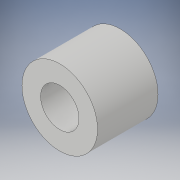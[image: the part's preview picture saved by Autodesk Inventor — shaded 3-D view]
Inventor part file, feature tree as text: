
AUTODESK INVENTOR PART (.ipt)
format: ipt  version: 2018 (Build 220112000, 112)  size: 107,520 bytes
history: native  units: in
note: dims shown in document units (in); Inventor stores cm internally (conversion verified against a paired STEP export)
features: sketch x2, extrude x1, hole x1
ambient origin geometry x8: Origin, YZ Plane, XZ Plane, XY Plane, X Axis, Y Axis, Z Axis, Center Point
bodies: Solid1 (feature_tree)
feature tree (4):
  extrude  "Extrusion1"  Depth=0.5in
  hole  "Hole2"  [1 undecoded]
  sketch  "Sketch1"  dims[d0=0.9843in d1=0.5in]
  sketch  "Sketch3"  dims[d2=0.7874in d3=0.0in d11=0.1181in d12=0.196in d13=0.5in d14=0.375in d15=0.25in d16=0.5635in d17=0.75in d18=0.8108in]
note: 1 required parameter value undecoded (feature->parameter linkage not recoverable at this tier; creation-order binding heuristic only, values carry confidence <= 0.55)
